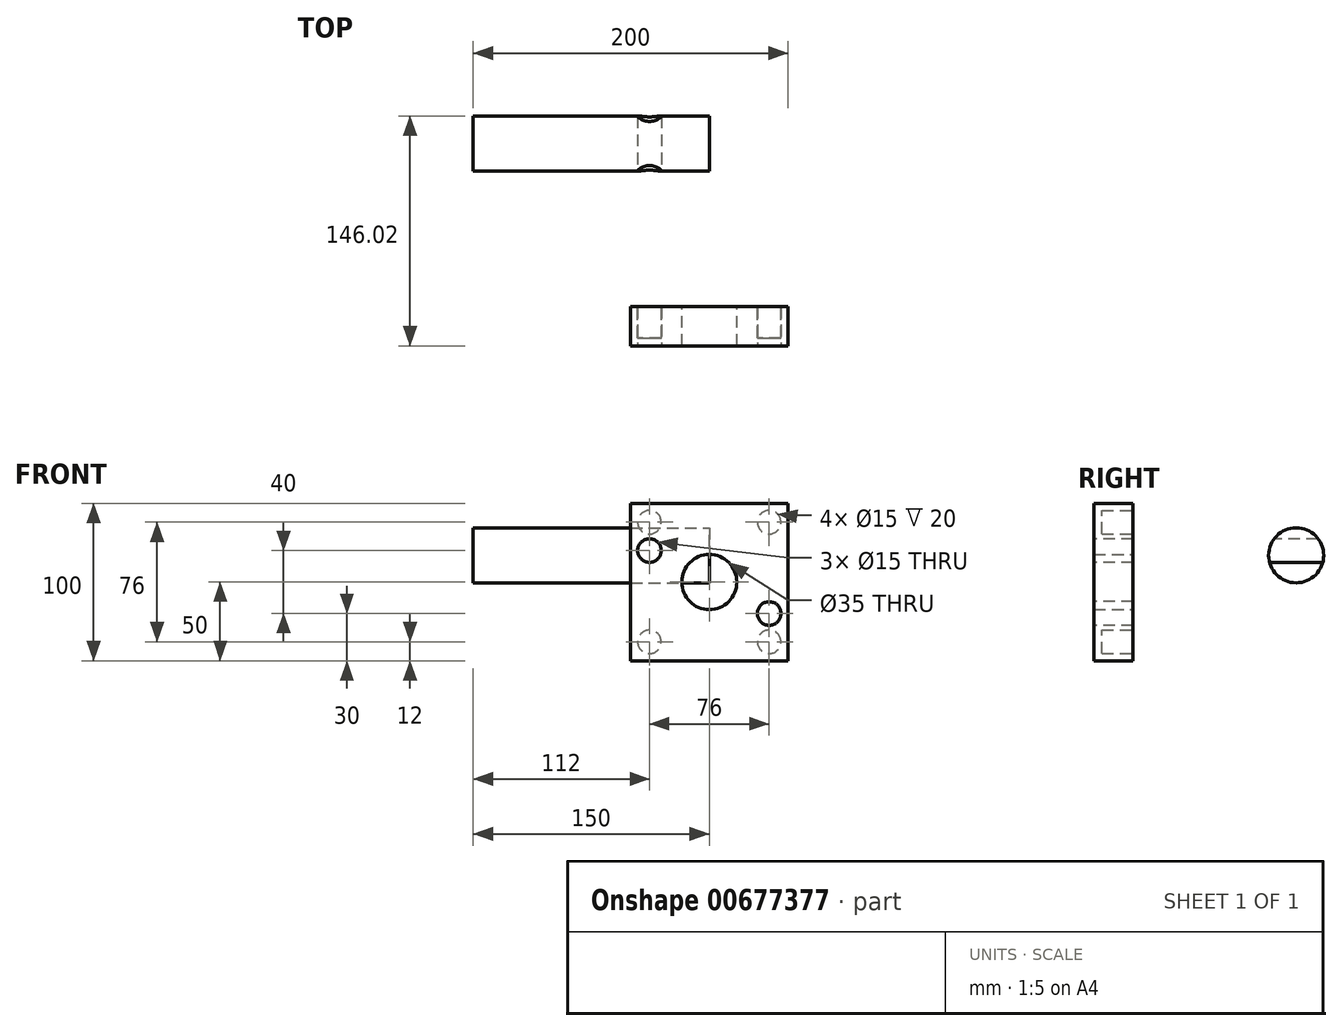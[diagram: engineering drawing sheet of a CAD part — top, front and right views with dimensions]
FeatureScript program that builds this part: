
annotation { "Feature Type Name" : "Feature", "Feature Type Description" : "" }
export const myFeature = defineFeature(function(context is Context, id is Id, definition is map)
    precondition{}
    {
        {
            var Q0;
            Q0=qCreatedBy(makeId("Front.planeOp"),FACE);
            var sketch = newSketch(context, id + "F0", { "sketchPlane" : qUnion([Q0])});
            skLineSegment(sketch, "E0.bottom", {"start": v(50, 50) * mm, "end": v(-50, 50) * mm});
            skLineSegment(sketch, "E0.top", {"start": v(50, -50) * mm, "end": v(-50, -50) * mm});
            skLineSegment(sketch, "E0.left", {"start": v(50, 50) * mm, "end": v(50, -50) * mm});
            skLineSegment(sketch, "E0.right", {"start": v(-50, 50) * mm, "end": v(-50, -50) * mm});
            skPoint(sketch, "E0.middle", {"position": v(0, 0) * mm});
            skCircle(sketch, "E1", {"center": v(0, 0) * mm, "radius": 17.5 * mm});
            skCircle(sketch, "E2", {"center": v(38, 38) * mm, "radius": 7.5 * mm});
            skCircle(sketch, "E3.1.0", {"center": v(-38, 38) * mm, "radius": 7.5 * mm});
            skCircle(sketch, "E3.2.0", {"center": v(-38, -38) * mm, "radius": 7.5 * mm});
            skCircle(sketch, "E3.3.0", {"center": v(38, -38) * mm, "radius": 7.5 * mm});
            skSolve(sketch);
        }
        {
            var Q0;
            Q0 = qSketchRegion(id + "F0", true);
            extrude(context, id + "F1", {"entities" : qUnion([Q0]), "depth" : 25 * mm, "offsetDistance" : 25 * mm});
        }
        {
            var Q0;
            Q0=qCreatedBy(makeId("Right.planeOp"),FACE);
            var sketch = newSketch(context, id + "F2", { "sketchPlane" : qUnion([Q0])});
            skCircle(sketch, "E4", {"center": v(103.52, 16.97) * mm, "radius": 17.5 * mm});
            skSolve(sketch);
        }
        {
            var Q0;
            Q0 = qSketchRegion(id + "F2", true);
            extrude(context, id + "F3", {"entities" : qUnion([Q0]), "oppositeDirection" : true, "depth" : 150 * mm, "offsetDistance" : 25 * mm});
        }
        {
            var Q0;
            Q0=makeQuery(id+"F1.opExtrude","CAP_FACE",FACE,{"disambiguationData":[OSD([sQuery(id+"F0.wireOp",EDGE,"E0.bottom"),sQuery(id+"F0.wireOp",EDGE,"E0.top"),sQuery(id+"F0.wireOp",EDGE,"E0.left"),sQuery(id+"F0.wireOp",EDGE,"E0.right"),sQuery(id+"F0.wireOp",EDGE,"E1"),sQuery(id+"F0.wireOp",EDGE,"E2"),sQuery(id+"F0.wireOp",EDGE,"E3.1.0"),sQuery(id+"F0.wireOp",EDGE,"E3.2.0"),sQuery(id+"F0.wireOp",EDGE,"E3.3.0")])],"isStart":false});
            var sketch = newSketch(context, id + "F4", { "sketchPlane" : qUnion([Q0])});
            skCircle(sketch, "E5.0", {"center": v(-38, 38) * mm, "radius": 7.5 * mm});
            skCircle(sketch, "E6.0", {"center": v(38, 38) * mm, "radius": 7.5 * mm});
            skCircle(sketch, "E7.0", {"center": v(38, -38) * mm, "radius": 7.5 * mm});
            skCircle(sketch, "E8.0", {"center": v(-38, -38) * mm, "radius": 7.5 * mm});
            skSolve(sketch);
        }
        {
            var Q0;
            Q0 = qSketchRegion(id + "F4", true);
            extrude(context, id + "F5", {"entities" : qUnion([Q0]), "operationType" : NewBodyOperationType.ADD, "oppositeDirection" : true, "depth" : 5 * mm, "offsetDistance" : 25 * mm});
        }
        {
            var Q0;
            Q0=makeQuery(id+"F5.boolean.opBoolean","MERGE",FACE,{"derivedFrom":[makeQuery(id+"F1.opExtrude","CAP_FACE",FACE,{"disambiguationData":[OSD([sQuery(id+"F0.wireOp",EDGE,"E0.bottom"),sQuery(id+"F0.wireOp",EDGE,"E0.top"),sQuery(id+"F0.wireOp",EDGE,"E0.left"),sQuery(id+"F0.wireOp",EDGE,"E0.right"),sQuery(id+"F0.wireOp",EDGE,"E1"),sQuery(id+"F0.wireOp",EDGE,"E2"),sQuery(id+"F0.wireOp",EDGE,"E3.1.0"),sQuery(id+"F0.wireOp",EDGE,"E3.2.0"),sQuery(id+"F0.wireOp",EDGE,"E3.3.0")])],"isStart":false}),makeQuery(id+"F5.opExtrude","CAP_FACE",FACE,{"disambiguationData":[OSD([sQuery(id+"F4.wireOp",EDGE,"E5.0")])],"isStart":true}),makeQuery(id+"F5.opExtrude","CAP_FACE",FACE,{"disambiguationData":[OSD([sQuery(id+"F4.wireOp",EDGE,"E6.0")])],"isStart":true}),makeQuery(id+"F5.opExtrude","CAP_FACE",FACE,{"disambiguationData":[OSD([sQuery(id+"F4.wireOp",EDGE,"E7.0")])],"isStart":true}),makeQuery(id+"F5.opExtrude","CAP_FACE",FACE,{"disambiguationData":[OSD([sQuery(id+"F4.wireOp",EDGE,"E8.0")])],"isStart":true})]});
            var sketch = newSketch(context, id + "F6", { "sketchPlane" : qUnion([Q0])});
            skCircle(sketch, "E9", {"center": v(-38, 20) * mm, "radius": 7.5 * mm});
            skCircle(sketch, "E10", {"center": v(38, -20) * mm, "radius": 7.5 * mm});
            skSolve(sketch);
        }
        {
            var Q0;
            Q0 = qSketchRegion(id + "F6", true);
            extrude(context, id + "F7", {"entities" : qUnion([Q0]), "operationType" : NewBodyOperationType.REMOVE, "endBound" : BoundingType.THROUGH_ALL, "oppositeDirection" : true, "depth" : 25 * mm, "offsetDistance" : 25 * mm});
        }
    });
